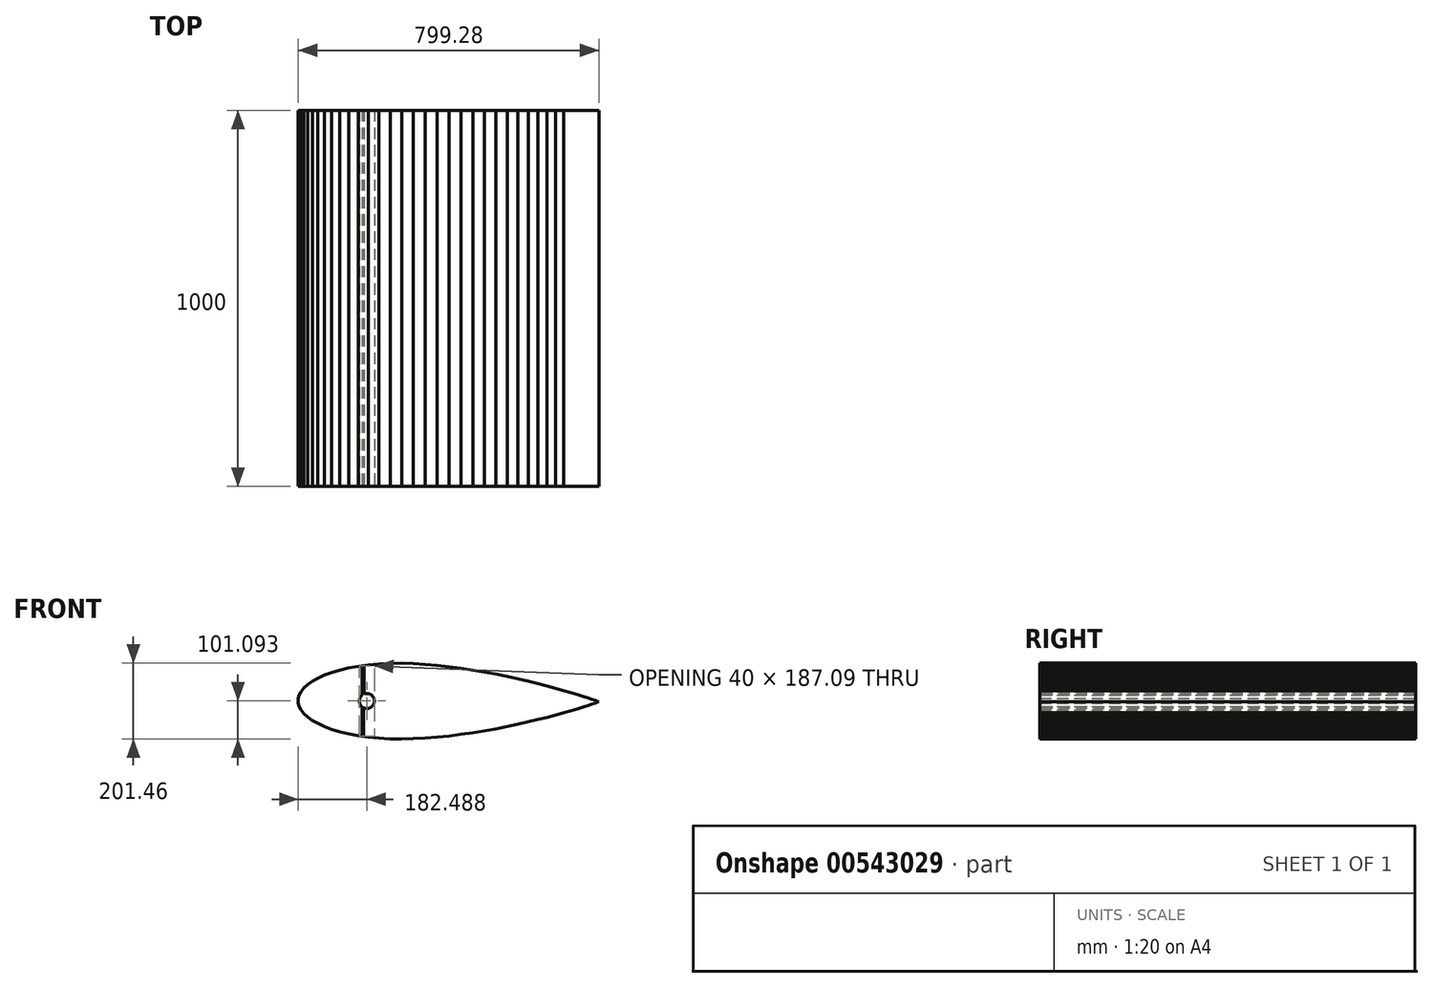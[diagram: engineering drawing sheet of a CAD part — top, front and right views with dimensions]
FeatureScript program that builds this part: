
annotation { "Feature Type Name" : "Feature", "Feature Type Description" : "" }
export const myFeature = defineFeature(function(context is Context, id is Id, definition is map)
    precondition{}
    {
        {
            var Q0;
            Q0=qCreatedBy(makeId("Front.planeOp"),FACE);
            var sketch = newSketch(context, id + "F0", { "sketchPlane" : qUnion([Q0])});
            skLineSegment(sketch, "E0", {"start": v(399.18, -21.9) * mm, "end": v(398.86, -21.79) * mm});
            skLineSegment(sketch, "E1", {"start": v(398.86, -21.79) * mm, "end": v(395.25, -20.53) * mm});
            skLineSegment(sketch, "E2", {"start": v(395.25, -20.53) * mm, "end": v(389.27, -18.47) * mm});
            skLineSegment(sketch, "E3", {"start": v(389.27, -18.47) * mm, "end": v(380.92, -15.64) * mm});
            skLineSegment(sketch, "E4", {"start": v(380.92, -15.64) * mm, "end": v(370.28, -12.1) * mm});
            skLineSegment(sketch, "E5", {"start": v(370.28, -12.1) * mm, "end": v(357.39, -7.88) * mm});
            skLineSegment(sketch, "E6", {"start": v(357.39, -7.88) * mm, "end": v(342.3, -3.1) * mm});
            skLineSegment(sketch, "E7", {"start": v(342.3, -3.1) * mm, "end": v(325.12, 2.2) * mm});
            skLineSegment(sketch, "E8", {"start": v(325.12, 2.2) * mm, "end": v(305.94, 7.9) * mm});
            skLineSegment(sketch, "E9", {"start": v(305.94, 7.9) * mm, "end": v(284.86, 13.92) * mm});
            skLineSegment(sketch, "E10", {"start": v(284.86, 13.92) * mm, "end": v(262, 20.19) * mm});
            skLineSegment(sketch, "E11", {"start": v(262, 20.19) * mm, "end": v(237.48, 26.58) * mm});
            skLineSegment(sketch, "E12", {"start": v(237.48, 26.58) * mm, "end": v(211.46, 33.03) * mm});
            skLineSegment(sketch, "E13", {"start": v(211.46, 33.03) * mm, "end": v(184.1, 39.41) * mm});
            skLineSegment(sketch, "E14", {"start": v(184.1, 39.41) * mm, "end": v(155.54, 45.66) * mm});
            skLineSegment(sketch, "E15", {"start": v(155.54, 45.66) * mm, "end": v(125.96, 51.68) * mm});
            skLineSegment(sketch, "E16", {"start": v(125.96, 51.68) * mm, "end": v(95.56, 57.36) * mm});
            skLineSegment(sketch, "E17", {"start": v(95.56, 57.36) * mm, "end": v(64.5, 62.64) * mm});
            skLineSegment(sketch, "E18", {"start": v(64.5, 62.64) * mm, "end": v(33, 67.41) * mm});
            skLineSegment(sketch, "E19", {"start": v(33, 67.41) * mm, "end": v(1.24, 71.6) * mm});
            skLineSegment(sketch, "E20", {"start": v(1.24, 71.6) * mm, "end": v(-30.58, 75.12) * mm});
            skLineSegment(sketch, "E21", {"start": v(-30.58, 75.12) * mm, "end": v(-62.24, 77.9) * mm});
            skLineSegment(sketch, "E22", {"start": v(-62.24, 77.9) * mm, "end": v(-93.8, 79.86) * mm});
            skLineSegment(sketch, "E23", {"start": v(-93.8, 79.86) * mm, "end": v(-125.17, 80.74) * mm});
            skLineSegment(sketch, "E24", {"start": v(-125.17, 80.74) * mm, "end": v(-155.75, 80.48) * mm});
            skLineSegment(sketch, "E25", {"start": v(-155.75, 80.48) * mm, "end": v(-185.33, 79.08) * mm});
            skLineSegment(sketch, "E26", {"start": v(-185.33, 79.08) * mm, "end": v(-213.7, 76.53) * mm});
            skLineSegment(sketch, "E27", {"start": v(-213.7, 76.53) * mm, "end": v(-240.64, 72.9) * mm});
            skLineSegment(sketch, "E28", {"start": v(-240.64, 72.9) * mm, "end": v(-265.96, 68.24) * mm});
            skLineSegment(sketch, "E29", {"start": v(-265.96, 68.24) * mm, "end": v(-289.48, 62.61) * mm});
            skLineSegment(sketch, "E30", {"start": v(-289.48, 62.61) * mm, "end": v(-311.05, 56.12) * mm});
            skLineSegment(sketch, "E31", {"start": v(-311.05, 56.12) * mm, "end": v(-330.52, 48.9) * mm});
            skLineSegment(sketch, "E32", {"start": v(-330.52, 48.9) * mm, "end": v(-347.75, 41.02) * mm});
            skLineSegment(sketch, "E33", {"start": v(-347.75, 41.02) * mm, "end": v(-362.66, 32.64) * mm});
            skLineSegment(sketch, "E34", {"start": v(-362.66, 32.64) * mm, "end": v(-375.16, 23.87) * mm});
            skLineSegment(sketch, "E35", {"start": v(-375.16, 23.87) * mm, "end": v(-385.18, 14.83) * mm});
            skLineSegment(sketch, "E36", {"start": v(-385.18, 14.83) * mm, "end": v(-392.68, 5.62) * mm});
            skLineSegment(sketch, "E37", {"start": v(-392.68, 5.62) * mm, "end": v(-397.64, -3.66) * mm});
            skLineSegment(sketch, "E38", {"start": v(-397.64, -3.66) * mm, "end": v(-400.06, -12.95) * mm});
            skLineSegment(sketch, "E39", {"start": v(-400.06, -12.95) * mm, "end": v(-399.98, -19) * mm});
            skLineSegment(sketch, "E40", {"start": v(483.26, -22.2) * mm, "end": v(399.18, -21.9) * mm});
            skPoint(sketch, "E41.orphan", {"position": v(-399.94, -22.2) * mm});
            skPoint(sketch, "E42.orphan", {"position": v(400.06, -22.2) * mm});
            skLineSegment(sketch, "E43.MirrorCS", {"start": v(-400.1, -25.04) * mm, "end": v(-399.98, -19) * mm});
            skLineSegment(sketch, "E44.MirrorCS", {"start": v(-397.76, -34.35) * mm, "end": v(-400.1, -25.04) * mm});
            skLineSegment(sketch, "E45.MirrorCS", {"start": v(-385.43, -52.92) * mm, "end": v(-392.86, -43.66) * mm});
            skLineSegment(sketch, "E46.MirrorCS", {"start": v(-375.47, -62.04) * mm, "end": v(-385.43, -52.92) * mm});
            skLineSegment(sketch, "E47.MirrorCS", {"start": v(-363.04, -70.9) * mm, "end": v(-375.47, -62.04) * mm});
            skLineSegment(sketch, "E48.MirrorCS", {"start": v(-392.86, -43.66) * mm, "end": v(-397.76, -34.35) * mm});
            skLineSegment(sketch, "E49.MirrorCS", {"start": v(-348.19, -79.39) * mm, "end": v(-363.04, -70.9) * mm});
            skLineSegment(sketch, "E50.MirrorCS", {"start": v(-331.01, -87.38) * mm, "end": v(-348.19, -79.39) * mm});
            skLineSegment(sketch, "E51.MirrorCS", {"start": v(-311.6, -94.76) * mm, "end": v(-331.01, -87.38) * mm});
            skLineSegment(sketch, "E52.MirrorCS", {"start": v(-290.08, -101.4) * mm, "end": v(-311.6, -94.76) * mm});
            skLineSegment(sketch, "E53.MirrorCS", {"start": v(-266.6, -107.2) * mm, "end": v(-290.08, -101.4) * mm});
            skLineSegment(sketch, "E54.MirrorCS", {"start": v(-241.3, -112.05) * mm, "end": v(-266.6, -107.2) * mm});
            skLineSegment(sketch, "E55.MirrorCS", {"start": v(-214.4, -115.87) * mm, "end": v(-241.3, -112.05) * mm});
            skLineSegment(sketch, "E56.MirrorCS", {"start": v(-186.05, -118.62) * mm, "end": v(-214.4, -115.87) * mm});
            skLineSegment(sketch, "E57.MirrorCS", {"start": v(-156.48, -120.25) * mm, "end": v(-186.05, -118.62) * mm});
            skLineSegment(sketch, "E58.MirrorCS", {"start": v(-125.9, -120.72) * mm, "end": v(-156.48, -120.25) * mm});
            skLineSegment(sketch, "E59.MirrorCS", {"start": v(-94.53, -120.07) * mm, "end": v(-125.9, -120.72) * mm});
            skLineSegment(sketch, "E60.MirrorCS", {"start": v(-62.95, -118.35) * mm, "end": v(-94.53, -120.07) * mm});
            skLineSegment(sketch, "E61.MirrorCS", {"start": v(-31.27, -115.8) * mm, "end": v(-62.95, -118.35) * mm});
            skLineSegment(sketch, "E62.MirrorCS", {"start": v(0.57, -112.5) * mm, "end": v(-31.27, -115.8) * mm});
            skLineSegment(sketch, "E63.MirrorCS", {"start": v(32.36, -108.55) * mm, "end": v(0.57, -112.5) * mm});
            skLineSegment(sketch, "E64.MirrorCS", {"start": v(63.9, -104) * mm, "end": v(32.36, -108.55) * mm});
            skLineSegment(sketch, "E65.MirrorCS", {"start": v(94.99, -98.95) * mm, "end": v(63.9, -104) * mm});
            skLineSegment(sketch, "E66.MirrorCS", {"start": v(125.44, -93.49) * mm, "end": v(94.99, -98.95) * mm});
            skLineSegment(sketch, "E67.MirrorCS", {"start": v(155.06, -87.68) * mm, "end": v(125.44, -93.49) * mm});
            skLineSegment(sketch, "E68.MirrorCS", {"start": v(183.65, -81.64) * mm, "end": v(155.06, -87.68) * mm});
            skLineSegment(sketch, "E69.MirrorCS", {"start": v(211.07, -75.46) * mm, "end": v(183.65, -81.64) * mm});
            skLineSegment(sketch, "E70.MirrorCS", {"start": v(237.13, -69.2) * mm, "end": v(211.07, -75.46) * mm});
            skLineSegment(sketch, "E71.MirrorCS", {"start": v(261.7, -62.99) * mm, "end": v(237.13, -69.2) * mm});
            skLineSegment(sketch, "E72.MirrorCS", {"start": v(284.6, -56.89) * mm, "end": v(261.7, -62.99) * mm});
            skLineSegment(sketch, "E73.MirrorCS", {"start": v(324.95, -45.45) * mm, "end": v(305.73, -51.02) * mm});
            skLineSegment(sketch, "E74.MirrorCS", {"start": v(305.73, -51.02) * mm, "end": v(284.6, -56.89) * mm});
            skLineSegment(sketch, "E75.MirrorCS", {"start": v(342.17, -40.3) * mm, "end": v(324.95, -45.45) * mm});
            skLineSegment(sketch, "E76.MirrorCS", {"start": v(357.29, -35.6) * mm, "end": v(342.17, -40.3) * mm});
            skLineSegment(sketch, "E77.MirrorCS", {"start": v(370.21, -31.5) * mm, "end": v(357.29, -35.6) * mm});
            skLineSegment(sketch, "E78.MirrorCS", {"start": v(380.88, -28.03) * mm, "end": v(370.21, -31.5) * mm});
            skLineSegment(sketch, "E79.MirrorCS", {"start": v(389.24, -25.26) * mm, "end": v(380.88, -28.03) * mm});
            skLineSegment(sketch, "E80.MirrorCS", {"start": v(395.24, -23.24) * mm, "end": v(389.24, -25.26) * mm});
            skLineSegment(sketch, "E81.MirrorCS", {"start": v(398.86, -22) * mm, "end": v(395.24, -23.24) * mm});
            skLineSegment(sketch, "E82.MirrorCS", {"start": v(399.18, -21.9) * mm, "end": v(398.86, -22) * mm});
            skPoint(sketch, "E83.MirrorCS.end.orphan", {"position": v(-213.8, -33.39) * mm});
            skPoint(sketch, "E83.MirrorCS.start.orphan", {"position": v(-214.4, -115.87) * mm});
            skPoint(sketch, "E84.MirrorCS.end.orphan", {"position": v(-227.26, -32.67) * mm});
            skPoint(sketch, "E84.MirrorCS.start.orphan", {"position": v(-227.85, -113.96) * mm});
            skPoint(sketch, "E85.end.orphan", {"position": v(-227.16, -6.58) * mm});
            skPoint(sketch, "E85.start.orphan", {"position": v(-227.16, 74.72) * mm});
            skPoint(sketch, "E86.end.orphan", {"position": v(-213.7, -5.95) * mm});
            skPoint(sketch, "E87.start.orphan", {"position": v(-320.78, 52.5) * mm});
            skLineSegment(sketch, "E88.trimOffspring", {"start": v(-399.98, -19) * mm, "end": v(-545.03, -18.47) * mm});
            skSolve(sketch);
        }
        {
            var Q0;
            Q0=makeQuery(id+"F0.imprint","IMPRINT",FACE,{"disambiguationData":[TD([[makeQuery(id+"F0.imprint","IMPRINT",EDGE,{"derivedFrom":sQuery(id+"F0.wireOp",EDGE,"E0")}),1.0]])]});
            extrude(context, id + "F1", {"entities" : qUnion([Q0]), "depth" : 1000 * mm, "offsetDistance" : 25 * mm});
        }
        {
            var Q0;
            Q0=makeQuery(id+"F1.opExtrude","CAP_FACE",FACE,{"disambiguationData":[OSD([sQuery(id+"F0.wireOp",EDGE,"E0"),sQuery(id+"F0.wireOp",EDGE,"E1"),sQuery(id+"F0.wireOp",EDGE,"E2"),sQuery(id+"F0.wireOp",EDGE,"E3"),sQuery(id+"F0.wireOp",EDGE,"E4"),sQuery(id+"F0.wireOp",EDGE,"E5"),sQuery(id+"F0.wireOp",EDGE,"E6"),sQuery(id+"F0.wireOp",EDGE,"E7"),sQuery(id+"F0.wireOp",EDGE,"E8"),sQuery(id+"F0.wireOp",EDGE,"E9"),sQuery(id+"F0.wireOp",EDGE,"E10"),sQuery(id+"F0.wireOp",EDGE,"E11"),sQuery(id+"F0.wireOp",EDGE,"E12"),sQuery(id+"F0.wireOp",EDGE,"E13"),sQuery(id+"F0.wireOp",EDGE,"E14"),sQuery(id+"F0.wireOp",EDGE,"E15"),sQuery(id+"F0.wireOp",EDGE,"E16"),sQuery(id+"F0.wireOp",EDGE,"E17"),sQuery(id+"F0.wireOp",EDGE,"E18"),sQuery(id+"F0.wireOp",EDGE,"E19"),sQuery(id+"F0.wireOp",EDGE,"E20"),sQuery(id+"F0.wireOp",EDGE,"E21"),sQuery(id+"F0.wireOp",EDGE,"E22"),sQuery(id+"F0.wireOp",EDGE,"E23"),sQuery(id+"F0.wireOp",EDGE,"E24"),sQuery(id+"F0.wireOp",EDGE,"E25"),sQuery(id+"F0.wireOp",EDGE,"E26"),sQuery(id+"F0.wireOp",EDGE,"E27"),sQuery(id+"F0.wireOp",EDGE,"E28"),sQuery(id+"F0.wireOp",EDGE,"E29"),sQuery(id+"F0.wireOp",EDGE,"E30"),sQuery(id+"F0.wireOp",EDGE,"E31"),sQuery(id+"F0.wireOp",EDGE,"E32"),sQuery(id+"F0.wireOp",EDGE,"E33"),sQuery(id+"F0.wireOp",EDGE,"E34"),sQuery(id+"F0.wireOp",EDGE,"E35"),sQuery(id+"F0.wireOp",EDGE,"E36"),sQuery(id+"F0.wireOp",EDGE,"E37"),sQuery(id+"F0.wireOp",EDGE,"E38"),sQuery(id+"F0.wireOp",EDGE,"E39"),sQuery(id+"F0.wireOp",EDGE,"E43.MirrorCS"),sQuery(id+"F0.wireOp",EDGE,"E44.MirrorCS"),sQuery(id+"F0.wireOp",EDGE,"E45.MirrorCS"),sQuery(id+"F0.wireOp",EDGE,"E46.MirrorCS"),sQuery(id+"F0.wireOp",EDGE,"E48.MirrorCS"),sQuery(id+"F0.wireOp",EDGE,"E47.MirrorCS"),sQuery(id+"F0.wireOp",EDGE,"E49.MirrorCS"),sQuery(id+"F0.wireOp",EDGE,"E50.MirrorCS"),sQuery(id+"F0.wireOp",EDGE,"E51.MirrorCS"),sQuery(id+"F0.wireOp",EDGE,"E52.MirrorCS"),sQuery(id+"F0.wireOp",EDGE,"E53.MirrorCS"),sQuery(id+"F0.wireOp",EDGE,"E54.MirrorCS"),sQuery(id+"F0.wireOp",EDGE,"E55.MirrorCS"),sQuery(id+"F0.wireOp",EDGE,"E56.MirrorCS"),sQuery(id+"F0.wireOp",EDGE,"E57.MirrorCS"),sQuery(id+"F0.wireOp",EDGE,"E58.MirrorCS"),sQuery(id+"F0.wireOp",EDGE,"E59.MirrorCS"),sQuery(id+"F0.wireOp",EDGE,"E60.MirrorCS"),sQuery(id+"F0.wireOp",EDGE,"E61.MirrorCS"),sQuery(id+"F0.wireOp",EDGE,"E62.MirrorCS"),sQuery(id+"F0.wireOp",EDGE,"E63.MirrorCS"),sQuery(id+"F0.wireOp",EDGE,"E64.MirrorCS"),sQuery(id+"F0.wireOp",EDGE,"E65.MirrorCS"),sQuery(id+"F0.wireOp",EDGE,"E66.MirrorCS"),sQuery(id+"F0.wireOp",EDGE,"E67.MirrorCS"),sQuery(id+"F0.wireOp",EDGE,"E68.MirrorCS"),sQuery(id+"F0.wireOp",EDGE,"E69.MirrorCS"),sQuery(id+"F0.wireOp",EDGE,"E70.MirrorCS"),sQuery(id+"F0.wireOp",EDGE,"E71.MirrorCS"),sQuery(id+"F0.wireOp",EDGE,"E72.MirrorCS"),sQuery(id+"F0.wireOp",EDGE,"E73.MirrorCS"),sQuery(id+"F0.wireOp",EDGE,"E74.MirrorCS"),sQuery(id+"F0.wireOp",EDGE,"E75.MirrorCS"),sQuery(id+"F0.wireOp",EDGE,"E76.MirrorCS"),sQuery(id+"F0.wireOp",EDGE,"E77.MirrorCS"),sQuery(id+"F0.wireOp",EDGE,"E78.MirrorCS"),sQuery(id+"F0.wireOp",EDGE,"E79.MirrorCS"),sQuery(id+"F0.wireOp",EDGE,"E80.MirrorCS"),sQuery(id+"F0.wireOp",EDGE,"E81.MirrorCS"),sQuery(id+"F0.wireOp",EDGE,"E82.MirrorCS")])],"isStart":false});
            var sketch = newSketch(context, id + "F2", { "sketchPlane" : qUnion([Q0])});
            skLineSegment(sketch, "E89", {"start": v(-545.03, -18.47) * mm, "end": v(483.26, -22.2) * mm});
            skArc(sketch, "E90", {"start": v(-229.6, -3.65) * mm, "mid": v(-207.55, -36.94) * mm, "end": v(-225.6, -1.32) * mm});
            skLineSegment(sketch, "E91", {"start": v(-229.6, 73.38) * mm, "end": v(-225.6, 73.92) * mm});
            skLineSegment(sketch, "E92", {"start": v(-229.6, 73.38) * mm, "end": v(-229.6, -3.65) * mm});
            skLineSegment(sketch, "E93", {"start": v(-225.6, 73.92) * mm, "end": v(-225.6, -1.32) * mm});
            skPoint(sketch, "E94.end.orphan", {"position": v(-326.66, -19.26) * mm});
            skPoint(sketch, "E94.start.orphan", {"position": v(-326.66, 50.33) * mm});
            skPoint(sketch, "E95.end.orphan", {"position": v(-330.76, -19.25) * mm});
            skPoint(sketch, "E95.start.orphan", {"position": v(-330.52, 48.9) * mm});
            skPoint(sketch, "E96.MirrorCS.start.orphan", {"position": v(-327.16, -88.85) * mm});
            skPoint(sketch, "E97.MirrorCS.start.orphan", {"position": v(-331.01, -87.38) * mm});
            skLineSegment(sketch, "E98.MirrorCS", {"start": v(-226.28, -113.17) * mm, "end": v(-225.74, -37.93) * mm});
            skLineSegment(sketch, "E99.MirrorCS", {"start": v(-230.28, -112.6) * mm, "end": v(-229.72, -35.58) * mm});
            skLineSegment(sketch, "E100.MirrorCS", {"start": v(-230.28, -112.6) * mm, "end": v(-226.28, -113.17) * mm});
            skSolve(sketch);
        }
        {
            var Q0;
            Q0 = qSketchRegion(id + "F2", true);
            var Q1;
            {var subQ0=sQuery(id+"F2.wireOp",EDGE,"E95");Q1=makeQuery(id+"F2.imprint","IMPRINT",FACE,{"disambiguationData":[TD([[makeQuery(id+"F2.imprint","IMPRINT",EDGE,{"derivedFrom":subQ0}),1.0]])]});}
            var Q2;
            {var subQ2=sQuery(id+"F2.wireOp",EDGE,"E96.MirrorCS");Q2=makeQuery(id+"F2.imprint","IMPRINT",FACE,{"disambiguationData":[TD([[makeQuery(id+"F2.imprint","IMPRINT",EDGE,{"derivedFrom":subQ2}),1.0]])]});}
            var Q3;
            {var subQ0=sQuery(id+"F2.wireOp",EDGE,"3WIJXAzT-w1ju-dI1U-FbNh-X1s5A0z71UK7");Q3=makeQuery(id+"F2.imprint","IMPRINT",FACE,{"disambiguationData":[TD([[makeQuery(id+"F2.imprint","IMPRINT",EDGE,{"derivedFrom":subQ0}),-1.0]])]});}
            var Q4;
            {var subQ0=sQuery(id+"F2.wireOp",EDGE,"e6214d46-a7a5-4d38-b97c-ab4130c6805e0.MirrorCS");Q4=makeQuery(id+"F2.imprint","IMPRINT",FACE,{"disambiguationData":[TD([[makeQuery(id+"F2.imprint","IMPRINT",EDGE,{"derivedFrom":subQ0}),1.0]])]});}
            extrude(context, id + "F3", {"entities" : qUnion([Q0, Q1, Q2, Q3, Q4]), "operationType" : NewBodyOperationType.REMOVE, "oppositeDirection" : true, "depth" : 1000 * mm, "offsetDistance" : 25 * mm});
        }
        {
            var Q0;
            Q0 = qSketchRegion(id + "F2", true);
            extrude(context, id + "F4", {"entities" : qUnion([Q0]), "operationType" : NewBodyOperationType.REMOVE, "oppositeDirection" : true, "depth" : 1100 * mm, "offsetDistance" : 25 * mm});
        }
    });
